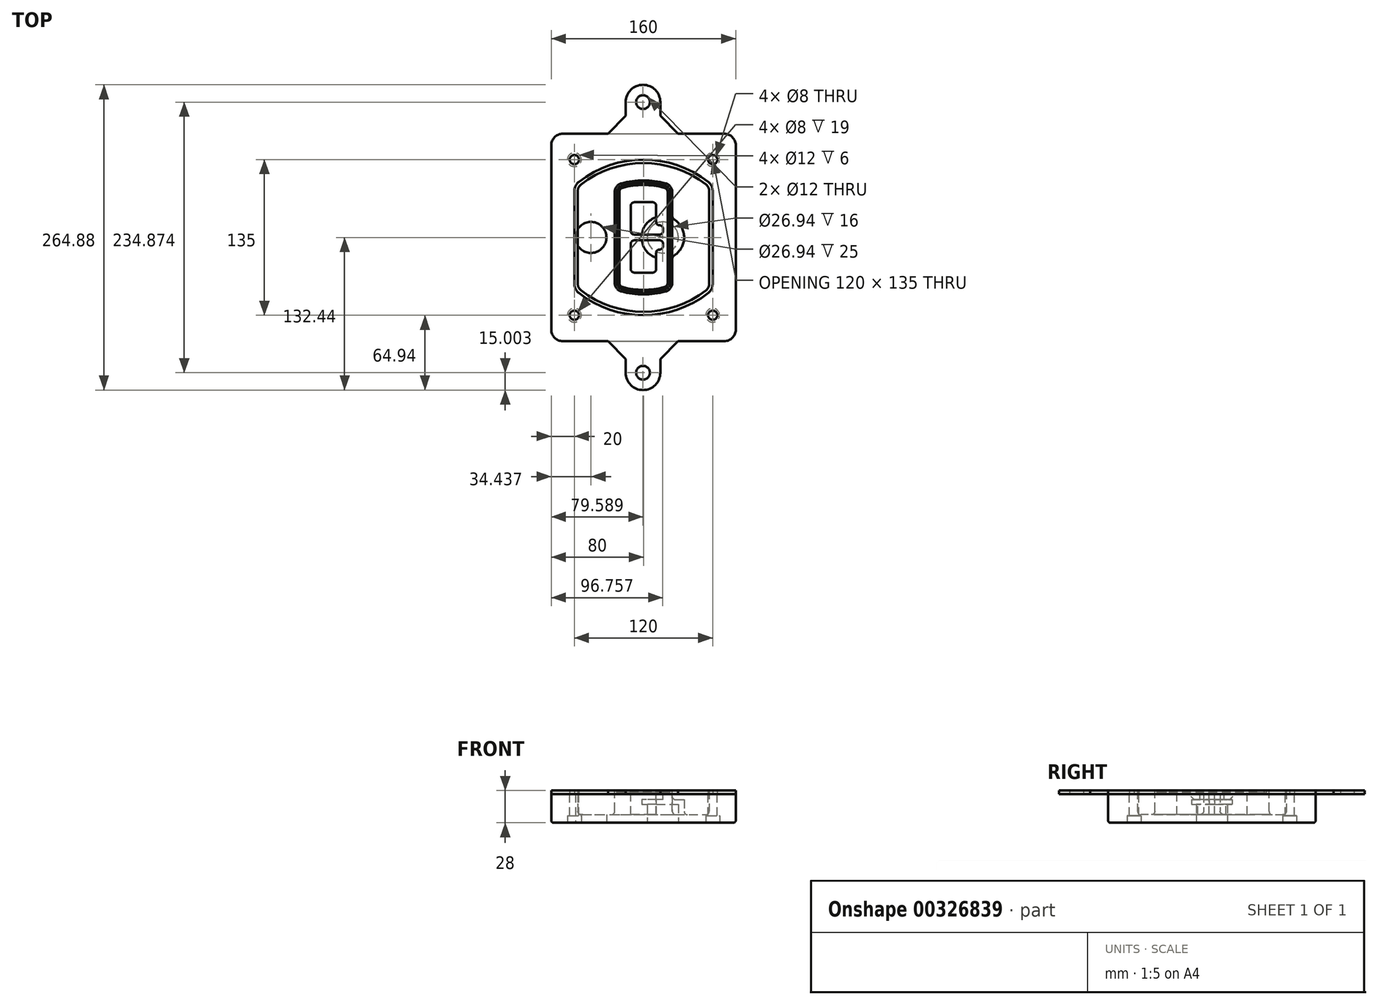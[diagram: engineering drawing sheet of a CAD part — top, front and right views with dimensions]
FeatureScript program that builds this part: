
annotation { "Feature Type Name" : "Feature", "Feature Type Description" : "" }
export const myFeature = defineFeature(function(context is Context, id is Id, definition is map)
    precondition{}
    {
        {
            var Q0;
            Q0=qCreatedBy(makeId("Top.planeOp"),FACE);
            var sketch = newSketch(context, id + "F0", { "sketchPlane" : qUnion([Q0])});
            skPoint(sketch, "E0.rect.middle", {"position": v(0, 0) * mm});
            skLineSegment(sketch, "E1.bottom", {"start": v(-70, -90) * mm, "end": v(70, -90) * mm});
            skLineSegment(sketch, "E1.top", {"start": v(-70, 90) * mm, "end": v(70, 90) * mm});
            skLineSegment(sketch, "E1.left", {"start": v(-80, -80) * mm, "end": v(-80, 80) * mm});
            skLineSegment(sketch, "E1.right", {"start": v(80, -80) * mm, "end": v(80, 80) * mm});
            skLineSegment(sketch, "E2", {"start": v(-80, 90) * mm, "end": v(80, -90) * mm, "construction": true});
            skLineSegment(sketch, "E3", {"start": v(80, 90) * mm, "end": v(-80, -90) * mm, "construction": true});
            skCircle(sketch, "E4", {"center": v(-60, 67.5) * mm, "radius": 4 * mm});
            skCircle(sketch, "E5", {"center": v(60, 67.5) * mm, "radius": 4 * mm});
            skCircle(sketch, "E6", {"center": v(60, -67.5) * mm, "radius": 4 * mm});
            skCircle(sketch, "E7", {"center": v(-60, -67.5) * mm, "radius": 4 * mm});
            skLineSegment(sketch, "E8", {"start": v(-60, 67.5) * mm, "end": v(60, 67.5) * mm, "construction": true});
            skLineSegment(sketch, "E9", {"start": v(60, 67.5) * mm, "end": v(60, -67.5) * mm, "construction": true});
            skLineSegment(sketch, "E10", {"start": v(60, -67.5) * mm, "end": v(-60, -67.5) * mm, "construction": true});
            skLineSegment(sketch, "E11", {"start": v(-60, -67.5) * mm, "end": v(-60, 67.5) * mm, "construction": true});
            skLineSegment(sketch, "E12", {"start": v(-60, 40.3) * mm, "end": v(-60, -40.3) * mm});
            skLineSegment(sketch, "E13", {"start": v(60, 40.3) * mm, "end": v(60, -40.3) * mm});
            skArc(sketch, "E14", {"start": v(56.15, 48.18) * mm, "mid": v(0, 67.5) * mm, "end": v(-56.15, 48.18) * mm});
            skArc(sketch, "E15", {"start": v(-56.15, -48.18) * mm, "mid": v(0, -67.5) * mm, "end": v(56.15, -48.18) * mm});
            skLineSegment(sketch, "E16", {"start": v(-60, 0) * mm, "end": v(60, 0) * mm, "construction": true});
            skPoint(sketch, "E17.visualSharp", {"position": v(-60, -45) * mm});
            skArc(sketch, "E17.filletArc", {"start": v(-60, -40.3) * mm, "mid": v(-58.99, -44.68) * mm, "end": v(-56.15, -48.18) * mm});
            skPoint(sketch, "E18.visualSharp", {"position": v(-60, 45) * mm});
            skArc(sketch, "E18.filletArc", {"start": v(-56.15, 48.18) * mm, "mid": v(-58.99, 44.68) * mm, "end": v(-60, 40.3) * mm});
            skPoint(sketch, "E19.visualSharp", {"position": v(60, 45) * mm});
            skArc(sketch, "E19.filletArc", {"start": v(60, 40.3) * mm, "mid": v(58.99, 44.68) * mm, "end": v(56.15, 48.18) * mm});
            skPoint(sketch, "E20.visualSharp", {"position": v(60, -45) * mm});
            skArc(sketch, "E20.filletArc", {"start": v(56.15, -48.18) * mm, "mid": v(58.99, -44.68) * mm, "end": v(60, -40.3) * mm});
            skPoint(sketch, "E21.visualSharp", {"position": v(-80, 90) * mm});
            skArc(sketch, "E21.filletArc", {"start": v(-70, 90) * mm, "mid": v(-77.07, 87.07) * mm, "end": v(-80, 80) * mm});
            skPoint(sketch, "E22.visualSharp", {"position": v(80, 90) * mm});
            skArc(sketch, "E22.filletArc", {"start": v(80, 80) * mm, "mid": v(77.07, 87.07) * mm, "end": v(70, 90) * mm});
            skPoint(sketch, "E23.visualSharp", {"position": v(80, -90) * mm});
            skArc(sketch, "E23.filletArc", {"start": v(70, -90) * mm, "mid": v(77.07, -87.07) * mm, "end": v(80, -80) * mm});
            skPoint(sketch, "E24.visualSharp", {"position": v(-80, -90) * mm});
            skArc(sketch, "E24.filletArc", {"start": v(-80, -80) * mm, "mid": v(-77.07, -87.07) * mm, "end": v(-70, -90) * mm});
            skArc(sketch, "E25.0", {"start": v(57, 40.3) * mm, "mid": v(56.3, 43.36) * mm, "end": v(54.3, 45.81) * mm});
            skLineSegment(sketch, "E25.1", {"start": v(57, 40.3) * mm, "end": v(57, -40.3) * mm});
            skArc(sketch, "E25.2", {"start": v(54.3, -45.81) * mm, "mid": v(56.3, -43.36) * mm, "end": v(57, -40.3) * mm});
            skArc(sketch, "E25.3", {"start": v(-54.3, -45.81) * mm, "mid": v(0, -64.5) * mm, "end": v(54.3, -45.81) * mm});
            skArc(sketch, "E25.4", {"start": v(-57, -40.3) * mm, "mid": v(-56.3, -43.36) * mm, "end": v(-54.3, -45.81) * mm});
            skArc(sketch, "E25.5", {"start": v(54.3, 45.81) * mm, "mid": v(0, 64.5) * mm, "end": v(-54.3, 45.81) * mm});
            skLineSegment(sketch, "E25.6", {"start": v(-57, 40.3) * mm, "end": v(-57, -40.3) * mm});
            skArc(sketch, "E25.7", {"start": v(-54.3, 45.81) * mm, "mid": v(-56.3, 43.36) * mm, "end": v(-57, 40.3) * mm});
            skArc(sketch, "E26.0", {"start": v(-58.62, 51.33) * mm, "mid": v(-62.58, 46.43) * mm, "end": v(-64, 40.3) * mm});
            skArc(sketch, "E26.1", {"start": v(58.62, 51.33) * mm, "mid": v(0, 71.5) * mm, "end": v(-58.62, 51.33) * mm});
            skArc(sketch, "E26.2", {"start": v(64, 40.3) * mm, "mid": v(62.58, 46.43) * mm, "end": v(58.62, 51.33) * mm});
            skLineSegment(sketch, "E26.3", {"start": v(64, 40.3) * mm, "end": v(64, -40.3) * mm});
            skArc(sketch, "E26.4", {"start": v(58.62, -51.33) * mm, "mid": v(62.58, -46.43) * mm, "end": v(64, -40.3) * mm});
            skLineSegment(sketch, "E26.5", {"start": v(-64, 40.3) * mm, "end": v(-64, -40.3) * mm});
            skArc(sketch, "E26.6", {"start": v(-58.62, -51.33) * mm, "mid": v(0, -71.5) * mm, "end": v(58.62, -51.33) * mm});
            skArc(sketch, "E26.7", {"start": v(-64, -40.3) * mm, "mid": v(-62.58, -46.43) * mm, "end": v(-58.62, -51.33) * mm});
            skSolve(sketch);
        }
        {
            var Q0;
            Q0=makeQuery(id+"F0.imprint","IMPRINT",FACE,{"disambiguationData":[TD([[makeQuery(id+"F0.imprint","IMPRINT",EDGE,{"derivedFrom":sQuery(id+"F0.wireOp",EDGE,"E1.bottom")}),1.0]])]});
            var Q1;
            Q1=makeQuery(id+"F0.imprint","IMPRINT",FACE,{"disambiguationData":[TD([[makeQuery(id+"F0.imprint","IMPRINT",EDGE,{"derivedFrom":sQuery(id+"F0.wireOp",EDGE,"E12")}),1.0]])]});
            var Q2;
            Q2=makeQuery(id+"F0.imprint","IMPRINT",FACE,{"disambiguationData":[TD([[makeQuery(id+"F0.imprint","IMPRINT",EDGE,{"derivedFrom":sQuery(id+"F0.wireOp",EDGE,"E25.0")}),1.0]])]});
            var Q3;
            Q3=makeQuery(id+"F0.imprint","IMPRINT",FACE,{"disambiguationData":[TD([[makeQuery(id+"F0.imprint","IMPRINT",EDGE,{"derivedFrom":sQuery(id+"F0.wireOp",EDGE,"E12")}),-1.0]])]});
            extrude(context, id + "F1", {"entities" : qUnion([Q0, Q1, Q2, Q3]), "oppositeDirection" : true, "depth" : 25 * mm});
        }
        {
            var Q0;
            Q0=makeQuery(id+"F0.imprint","IMPRINT",FACE,{"disambiguationData":[TD([[makeQuery(id+"F0.imprint","IMPRINT",EDGE,{"derivedFrom":sQuery(id+"F0.wireOp",EDGE,"E12")}),1.0]])]});
            extrude(context, id + "F2", {"entities" : qUnion([Q0]), "operationType" : NewBodyOperationType.ADD, "depth" : 3 * mm});
        }
        {
            var Q0;
            Q0=makeQuery(id+"F0.imprint","IMPRINT",FACE,{"disambiguationData":[TD([[makeQuery(id+"F0.imprint","IMPRINT",EDGE,{"derivedFrom":sQuery(id+"F0.wireOp",EDGE,"E25.0")}),1.0]])]});
            extrude(context, id + "F3", {"entities" : qUnion([Q0]), "operationType" : NewBodyOperationType.REMOVE, "oppositeDirection" : true, "depth" : 18 * mm});
        }
        {
            var Q0;
            Q0=makeQuery(id+"F2.opExtrude","CAP_FACE",FACE,{"disambiguationData":[OSD([sQuery(id+"F0.wireOp",EDGE,"E12"),sQuery(id+"F0.wireOp",EDGE,"E13"),sQuery(id+"F0.wireOp",EDGE,"E14"),sQuery(id+"F0.wireOp",EDGE,"E15"),sQuery(id+"F0.wireOp",EDGE,"E17.filletArc"),sQuery(id+"F0.wireOp",EDGE,"E18.filletArc"),sQuery(id+"F0.wireOp",EDGE,"E19.filletArc"),sQuery(id+"F0.wireOp",EDGE,"E20.filletArc"),sQuery(id+"F0.wireOp",EDGE,"E25.0"),sQuery(id+"F0.wireOp",EDGE,"E25.1"),sQuery(id+"F0.wireOp",EDGE,"E25.2"),sQuery(id+"F0.wireOp",EDGE,"E25.3"),sQuery(id+"F0.wireOp",EDGE,"E25.4"),sQuery(id+"F0.wireOp",EDGE,"E25.5"),sQuery(id+"F0.wireOp",EDGE,"E25.6"),sQuery(id+"F0.wireOp",EDGE,"E25.7")])],"isStart":false});
            var sketch = newSketch(context, id + "F4", { "sketchPlane" : qUnion([Q0])});
            skArc(sketch, "E27.0", {"start": v(-19.08, -46.97) * mm, "mid": v(0, -49.5) * mm, "end": v(19.08, -46.97) * mm});
            skArc(sketch, "E28.0", {"start": v(19.08, 46.97) * mm, "mid": v(0, 49.5) * mm, "end": v(-19.08, 46.97) * mm});
            skLineSegment(sketch, "E29", {"start": v(-25, 39.25) * mm, "end": v(-25, -39.25) * mm});
            skLineSegment(sketch, "E30", {"start": v(25, 39.25) * mm, "end": v(25, -39.25) * mm});
            skLineSegment(sketch, "E31", {"start": v(-25, 45.1) * mm, "end": v(25, 45.1) * mm, "construction": true});
            skLineSegment(sketch, "E32", {"start": v(-25, -45.1) * mm, "end": v(25, -45.1) * mm, "construction": true});
            skPoint(sketch, "E33.visualSharp", {"position": v(-25, 45.1) * mm});
            skArc(sketch, "E33.filletArc", {"start": v(-19.08, 46.97) * mm, "mid": v(-23.35, 44.11) * mm, "end": v(-25, 39.25) * mm});
            skPoint(sketch, "E34.visualSharp", {"position": v(25, 45.1) * mm});
            skArc(sketch, "E34.filletArc", {"start": v(25, 39.25) * mm, "mid": v(23.35, 44.11) * mm, "end": v(19.08, 46.97) * mm});
            skPoint(sketch, "E35.visualSharp", {"position": v(25, -45.1) * mm});
            skArc(sketch, "E35.filletArc", {"start": v(19.08, -46.97) * mm, "mid": v(23.35, -44.11) * mm, "end": v(25, -39.25) * mm});
            skPoint(sketch, "E36.visualSharp", {"position": v(-25, -45.1) * mm});
            skArc(sketch, "E36.filletArc", {"start": v(-25, -39.25) * mm, "mid": v(-23.35, -44.11) * mm, "end": v(-19.08, -46.97) * mm});
            skArc(sketch, "E37.0", {"start": v(54.3, 45.81) * mm, "mid": v(0, 64.5) * mm, "end": v(-54.3, 45.81) * mm});
            skArc(sketch, "E37.1", {"start": v(-54.3, 45.81) * mm, "mid": v(-56.3, 43.36) * mm, "end": v(-57, 40.3) * mm});
            skLineSegment(sketch, "E37.2", {"start": v(-57, 40.3) * mm, "end": v(-57, -40.3) * mm});
            skArc(sketch, "E37.3", {"start": v(-57, -40.3) * mm, "mid": v(-56.3, -43.36) * mm, "end": v(-54.3, -45.81) * mm});
            skArc(sketch, "E37.4", {"start": v(-54.3, -45.81) * mm, "mid": v(0, -64.5) * mm, "end": v(54.3, -45.81) * mm});
            skArc(sketch, "E37.5", {"start": v(54.3, -45.81) * mm, "mid": v(56.3, -43.36) * mm, "end": v(57, -40.3) * mm});
            skLineSegment(sketch, "E37.6", {"start": v(57, 40.3) * mm, "end": v(57, -40.3) * mm});
            skArc(sketch, "E37.7", {"start": v(57, 40.3) * mm, "mid": v(56.3, 43.36) * mm, "end": v(54.3, 45.81) * mm});
            skLineSegment(sketch, "E38.0", {"start": v(23, 39.25) * mm, "end": v(23, -39.25) * mm});
            skArc(sketch, "E38.1", {"start": v(18.56, -45.04) * mm, "mid": v(21.76, -42.9) * mm, "end": v(23, -39.25) * mm});
            skArc(sketch, "E38.2", {"start": v(-18.56, -45.04) * mm, "mid": v(0, -47.5) * mm, "end": v(18.56, -45.04) * mm});
            skArc(sketch, "E38.3", {"start": v(-23, -39.25) * mm, "mid": v(-21.76, -42.9) * mm, "end": v(-18.56, -45.04) * mm});
            skLineSegment(sketch, "E38.4", {"start": v(-23, 39.25) * mm, "end": v(-23, -39.25) * mm});
            skArc(sketch, "E38.5", {"start": v(23, 39.25) * mm, "mid": v(21.76, 42.9) * mm, "end": v(18.56, 45.04) * mm});
            skArc(sketch, "E38.6", {"start": v(-18.56, 45.04) * mm, "mid": v(-21.76, 42.9) * mm, "end": v(-23, 39.25) * mm});
            skArc(sketch, "E38.7", {"start": v(18.56, 45.04) * mm, "mid": v(0, 47.5) * mm, "end": v(-18.56, 45.04) * mm});
            skArc(sketch, "E39.0", {"start": v(21, 39.25) * mm, "mid": v(20.18, 41.68) * mm, "end": v(18.04, 43.1) * mm});
            skLineSegment(sketch, "E39.1", {"start": v(21, 39.25) * mm, "end": v(21, -39.25) * mm});
            skArc(sketch, "E39.2", {"start": v(18.04, -43.1) * mm, "mid": v(20.18, -41.68) * mm, "end": v(21, -39.25) * mm});
            skArc(sketch, "E39.3", {"start": v(-18.04, -43.1) * mm, "mid": v(0, -45.5) * mm, "end": v(18.04, -43.1) * mm});
            skArc(sketch, "E39.4", {"start": v(-21, -39.25) * mm, "mid": v(-20.18, -41.68) * mm, "end": v(-18.04, -43.1) * mm});
            skArc(sketch, "E39.5", {"start": v(18.04, 43.1) * mm, "mid": v(0, 45.5) * mm, "end": v(-18.04, 43.1) * mm});
            skLineSegment(sketch, "E39.6", {"start": v(-21, 39.25) * mm, "end": v(-21, -39.25) * mm});
            skArc(sketch, "E39.7", {"start": v(-18.04, 43.1) * mm, "mid": v(-20.18, 41.68) * mm, "end": v(-21, 39.25) * mm});
            skLineSegment(sketch, "E40", {"start": v(-25, 0) * mm, "end": v(25, 0) * mm, "construction": true});
            skLineSegment(sketch, "E41", {"start": v(-11, 5.5) * mm, "end": v(-11, 27.5) * mm});
            skLineSegment(sketch, "E42", {"start": v(-8, 30.5) * mm, "end": v(8, 30.5) * mm});
            skLineSegment(sketch, "E43", {"start": v(11, 27.5) * mm, "end": v(11, 13.5) * mm});
            skLineSegment(sketch, "E44", {"start": v(14, 10.5) * mm, "end": v(14, 10.5) * mm});
            skLineSegment(sketch, "E45", {"start": v(17, 7.5) * mm, "end": v(17, 5.5) * mm});
            skLineSegment(sketch, "E46", {"start": v(14, 2.5) * mm, "end": v(-8, 2.5) * mm});
            skPoint(sketch, "E47.visualSharp", {"position": v(-11, 30.5) * mm});
            skArc(sketch, "E47.filletArc", {"start": v(-8, 30.5) * mm, "mid": v(-10.12, 29.62) * mm, "end": v(-11, 27.5) * mm});
            skPoint(sketch, "E48.visualSharp", {"position": v(11, 30.5) * mm});
            skArc(sketch, "E48.filletArc", {"start": v(11, 27.5) * mm, "mid": v(10.12, 29.62) * mm, "end": v(8, 30.5) * mm});
            skPoint(sketch, "E49.visualSharp", {"position": v(11, 10.5) * mm});
            skArc(sketch, "E49.filletArc", {"start": v(11, 13.5) * mm, "mid": v(11.88, 11.38) * mm, "end": v(14, 10.5) * mm});
            skPoint(sketch, "E50.visualSharp", {"position": v(17, 10.5) * mm});
            skArc(sketch, "E50.filletArc", {"start": v(17, 7.5) * mm, "mid": v(16.12, 9.62) * mm, "end": v(14, 10.5) * mm});
            skPoint(sketch, "E51.visualSharp", {"position": v(17, 2.5) * mm});
            skArc(sketch, "E51.filletArc", {"start": v(14, 2.5) * mm, "mid": v(16.12, 3.38) * mm, "end": v(17, 5.5) * mm});
            skPoint(sketch, "E52.visualSharp", {"position": v(-11, 2.5) * mm});
            skArc(sketch, "E52.filletArc", {"start": v(-11, 5.5) * mm, "mid": v(-10.12, 3.38) * mm, "end": v(-8, 2.5) * mm});
            skLineSegment(sketch, "E53.0.MirrorCS", {"start": v(14, -2.5) * mm, "end": v(-8, -2.5) * mm});
            skArc(sketch, "E54.0.MirrorCS", {"start": v(-11, -5.5) * mm, "mid": v(-10.12, -3.38) * mm, "end": v(-8, -2.5) * mm});
            skLineSegment(sketch, "E55.0.MirrorCS", {"start": v(-11, -5.5) * mm, "end": v(-11, -27.5) * mm});
            skArc(sketch, "E56.0.MirrorCS", {"start": v(-8, -30.5) * mm, "mid": v(-10.12, -29.62) * mm, "end": v(-11, -27.5) * mm});
            skLineSegment(sketch, "E57.0.MirrorCS", {"start": v(-8, -30.5) * mm, "end": v(8, -30.5) * mm});
            skArc(sketch, "E58.0.MirrorCS", {"start": v(11, -27.5) * mm, "mid": v(10.12, -29.62) * mm, "end": v(8, -30.5) * mm});
            skLineSegment(sketch, "E59.0.MirrorCS", {"start": v(11, -27.5) * mm, "end": v(11, -13.5) * mm});
            skArc(sketch, "E60.0.MirrorCS", {"start": v(11, -13.5) * mm, "mid": v(11.88, -11.38) * mm, "end": v(14, -10.5) * mm});
            skArc(sketch, "E61.0.MirrorCS", {"start": v(17, -7.5) * mm, "mid": v(16.12, -9.62) * mm, "end": v(14, -10.5) * mm});
            skLineSegment(sketch, "E62.0.MirrorCS", {"start": v(17, -7.5) * mm, "end": v(17, -5.5) * mm});
            skArc(sketch, "E63.0.MirrorCS", {"start": v(14, -2.5) * mm, "mid": v(16.12, -3.38) * mm, "end": v(17, -5.5) * mm});
            skSolve(sketch);
        }
        {
            var Q0;
            Q0=makeQuery(id+"F4.imprint","IMPRINT",FACE,{"disambiguationData":[TD([[makeQuery(id+"F4.imprint","IMPRINT",EDGE,{"derivedFrom":sQuery(id+"F4.wireOp",EDGE,"E27.0")}),1.0]])]});
            var Q1;
            Q1=makeQuery(id+"F4.imprint","IMPRINT",FACE,{"disambiguationData":[TD([[makeQuery(id+"F4.imprint","IMPRINT",EDGE,{"derivedFrom":sQuery(id+"F4.wireOp",EDGE,"E38.0")}),-1.0]])]});
            var Q2;
            Q2=makeQuery(id+"F4.imprint","IMPRINT",FACE,{"disambiguationData":[TD([[makeQuery(id+"F4.imprint","IMPRINT",EDGE,{"derivedFrom":sQuery(id+"F4.wireOp",EDGE,"E39.0")}),1.0]])]});
            extrude(context, id + "F5", {"entities" : qUnion([Q0, Q1, Q2]), "operationType" : NewBodyOperationType.ADD, "endBound" : BoundingType.UP_TO_NEXT, "oppositeDirection" : true, "depth" : 25 * mm});
        }
        {
            var Q0;
            Q0=makeQuery(id+"F4.imprint","IMPRINT",FACE,{"disambiguationData":[TD([[makeQuery(id+"F4.imprint","IMPRINT",EDGE,{"derivedFrom":sQuery(id+"F4.wireOp",EDGE,"E38.0")}),-1.0]])]});
            extrude(context, id + "F6", {"entities" : qUnion([Q0]), "operationType" : NewBodyOperationType.REMOVE, "oppositeDirection" : true, "depth" : 2 * mm});
        }
        {
            var Q0;
            Q0=makeQuery(id+"F1.opExtrude","CAP_FACE",FACE,{"disambiguationData":[OSD([sQuery(id+"F0.wireOp",EDGE,"E1.bottom"),sQuery(id+"F0.wireOp",EDGE,"E1.top"),sQuery(id+"F0.wireOp",EDGE,"E1.left"),sQuery(id+"F0.wireOp",EDGE,"E1.right"),sQuery(id+"F0.wireOp",EDGE,"E4"),sQuery(id+"F0.wireOp",EDGE,"E5"),sQuery(id+"F0.wireOp",EDGE,"E6"),sQuery(id+"F0.wireOp",EDGE,"E7"),sQuery(id+"F0.wireOp",EDGE,"E21.filletArc"),sQuery(id+"F0.wireOp",EDGE,"E22.filletArc"),sQuery(id+"F0.wireOp",EDGE,"E23.filletArc"),sQuery(id+"F0.wireOp",EDGE,"E24.filletArc")])],"isStart":false});
            var sketch = newSketch(context, id + "F7", { "sketchPlane" : qUnion([Q0])});
            skCircle(sketch, "E64", {"center": v(16.76, 0) * mm, "radius": 13.47 * mm});
            skCircle(sketch, "E65", {"center": v(-45.56, 0) * mm, "radius": 13.47 * mm});
            skLineSegment(sketch, "E66", {"start": v(80, 0) * mm, "end": v(-80, 0) * mm});
            skCircle(sketch, "E67", {"center": v(16.76, 0) * mm, "radius": 18.47 * mm});
            skCircle(sketch, "E68", {"center": v(60, -67.5) * mm, "radius": 6 * mm});
            skCircle(sketch, "E69", {"center": v(-60, -67.5) * mm, "radius": 6 * mm});
            skCircle(sketch, "E70", {"center": v(-60, 67.5) * mm, "radius": 6 * mm});
            skCircle(sketch, "E71", {"center": v(60, 67.5) * mm, "radius": 6 * mm});
            skSolve(sketch);
        }
        {
            var Q0;
            {var subQ1=sQuery(id+"F7.wireOp",EDGE,"E66");var subQ4=sQuery(id+"F7.wireOp",EDGE,"E64");var subQ6=makeQuery(id+"F7.imprint","INTERSECT",VERTEX,{"disambiguationData":[OD(0.0)],"derivedFrom":[subQ4,subQ1]});Q0=makeQuery(id+"F7.imprint","IMPRINT",FACE,{"disambiguationData":[TD([[makeQuery(id+"F7.imprint","IMPRINT",EDGE,{"disambiguationData":[TD([[subQ6,-1.0]])],"derivedFrom":subQ4}),-1.0]])]});}
            var Q1;
            {var subQ0=sQuery(id+"F7.wireOp",EDGE,"E66");var subQ1=sQuery(id+"F7.wireOp",EDGE,"E64");var subQ3=makeQuery(id+"F7.imprint","INTERSECT",VERTEX,{"disambiguationData":[OD(0.0)],"derivedFrom":[subQ1,subQ0]});Q1=makeQuery(id+"F7.imprint","IMPRINT",FACE,{"disambiguationData":[TD([[makeQuery(id+"F7.imprint","IMPRINT",EDGE,{"disambiguationData":[TD([[subQ3,-1.0]])],"derivedFrom":subQ1}),1.0]])]});}
            var Q2;
            {var subQ0=sQuery(id+"F7.wireOp",EDGE,"E66");var subQ1=sQuery(id+"F7.wireOp",EDGE,"E64");var subQ3=makeQuery(id+"F7.imprint","INTERSECT",VERTEX,{"disambiguationData":[OD(0.0)],"derivedFrom":[subQ1,subQ0]});Q2=makeQuery(id+"F7.imprint","IMPRINT",FACE,{"disambiguationData":[TD([[makeQuery(id+"F7.imprint","IMPRINT",EDGE,{"disambiguationData":[TD([[subQ3,1.0]])],"derivedFrom":subQ1}),1.0]])]});}
            var Q3;
            {var subQ1=sQuery(id+"F7.wireOp",EDGE,"E66");var subQ4=sQuery(id+"F7.wireOp",EDGE,"E64");var subQ6=makeQuery(id+"F7.imprint","INTERSECT",VERTEX,{"disambiguationData":[OD(0.0)],"derivedFrom":[subQ4,subQ1]});Q3=makeQuery(id+"F7.imprint","IMPRINT",FACE,{"disambiguationData":[TD([[makeQuery(id+"F7.imprint","IMPRINT",EDGE,{"disambiguationData":[TD([[subQ6,1.0]])],"derivedFrom":subQ4}),-1.0]])]});}
            extrude(context, id + "F8", {"entities" : qUnion([Q0, Q1, Q2, Q3]), "operationType" : NewBodyOperationType.ADD, "oppositeDirection" : true, "depth" : 20 * mm});
        }
        {
            var Q0;
            {var subQ0=sQuery(id+"F7.wireOp",EDGE,"E66");var subQ1=sQuery(id+"F7.wireOp",EDGE,"E64");var subQ3=makeQuery(id+"F7.imprint","INTERSECT",VERTEX,{"disambiguationData":[OD(0.0)],"derivedFrom":[subQ1,subQ0]});Q0=makeQuery(id+"F7.imprint","IMPRINT",FACE,{"disambiguationData":[TD([[makeQuery(id+"F7.imprint","IMPRINT",EDGE,{"disambiguationData":[TD([[subQ3,-1.0]])],"derivedFrom":subQ1}),1.0]])]});}
            var Q1;
            {var subQ0=sQuery(id+"F7.wireOp",EDGE,"E66");var subQ1=sQuery(id+"F7.wireOp",EDGE,"E64");var subQ3=makeQuery(id+"F7.imprint","INTERSECT",VERTEX,{"disambiguationData":[OD(0.0)],"derivedFrom":[subQ1,subQ0]});Q1=makeQuery(id+"F7.imprint","IMPRINT",FACE,{"disambiguationData":[TD([[makeQuery(id+"F7.imprint","IMPRINT",EDGE,{"disambiguationData":[TD([[subQ3,1.0]])],"derivedFrom":subQ1}),1.0]])]});}
            extrude(context, id + "F9", {"entities" : qUnion([Q0, Q1]), "operationType" : NewBodyOperationType.REMOVE, "oppositeDirection" : true, "depth" : 16 * mm});
        }
        {
            var Q0;
            {var subQ0=sQuery(id+"F7.wireOp",EDGE,"E66");var subQ1=sQuery(id+"F7.wireOp",EDGE,"E65");var subQ3=makeQuery(id+"F7.imprint","INTERSECT",VERTEX,{"disambiguationData":[OD(0.0)],"derivedFrom":[subQ1,subQ0]});Q0=makeQuery(id+"F7.imprint","IMPRINT",FACE,{"disambiguationData":[TD([[makeQuery(id+"F7.imprint","IMPRINT",EDGE,{"disambiguationData":[TD([[subQ3,-1.0]])],"derivedFrom":subQ1}),1.0]])]});}
            var Q1;
            {var subQ0=sQuery(id+"F7.wireOp",EDGE,"E66");var subQ1=sQuery(id+"F7.wireOp",EDGE,"E65");var subQ3=makeQuery(id+"F7.imprint","INTERSECT",VERTEX,{"disambiguationData":[OD(0.0)],"derivedFrom":[subQ1,subQ0]});Q1=makeQuery(id+"F7.imprint","IMPRINT",FACE,{"disambiguationData":[TD([[makeQuery(id+"F7.imprint","IMPRINT",EDGE,{"disambiguationData":[TD([[subQ3,1.0]])],"derivedFrom":subQ1}),1.0]])]});}
            extrude(context, id + "F10", {"entities" : qUnion([Q0, Q1]), "operationType" : NewBodyOperationType.REMOVE, "oppositeDirection" : true, "depth" : 25 * mm});
        }
        {
            var Q0;
            Q0=makeQuery(id+"F7.imprint","IMPRINT",FACE,{"disambiguationData":[TD([[makeQuery(id+"F7.imprint","IMPRINT",EDGE,{"derivedFrom":sQuery(id+"F7.wireOp",EDGE,"E68")}),1.0]])]});
            var Q1;
            Q1=makeQuery(id+"F7.imprint","IMPRINT",FACE,{"disambiguationData":[TD([[makeQuery(id+"F7.imprint","IMPRINT",EDGE,{"derivedFrom":makeQuery(id+"F1.opExtrude","CAP_EDGE",EDGE,{"disambiguationData":[OSD([sQuery(id+"F0.wireOp",EDGE,"E5")])],"isStart":false})}),-1.0]])]});
            var Q2;
            Q2=makeQuery(id+"F7.imprint","IMPRINT",FACE,{"disambiguationData":[TD([[makeQuery(id+"F7.imprint","IMPRINT",EDGE,{"derivedFrom":sQuery(id+"F7.wireOp",EDGE,"E69")}),1.0]])]});
            var Q3;
            Q3=makeQuery(id+"F7.imprint","IMPRINT",FACE,{"disambiguationData":[TD([[makeQuery(id+"F7.imprint","IMPRINT",EDGE,{"derivedFrom":makeQuery(id+"F1.opExtrude","CAP_EDGE",EDGE,{"disambiguationData":[OSD([sQuery(id+"F0.wireOp",EDGE,"E4")])],"isStart":false})}),-1.0]])]});
            var Q4;
            Q4=makeQuery(id+"F7.imprint","IMPRINT",FACE,{"disambiguationData":[TD([[makeQuery(id+"F7.imprint","IMPRINT",EDGE,{"derivedFrom":sQuery(id+"F7.wireOp",EDGE,"E70")}),1.0]])]});
            var Q5;
            Q5=makeQuery(id+"F7.imprint","IMPRINT",FACE,{"disambiguationData":[TD([[makeQuery(id+"F7.imprint","IMPRINT",EDGE,{"derivedFrom":makeQuery(id+"F1.opExtrude","CAP_EDGE",EDGE,{"disambiguationData":[OSD([sQuery(id+"F0.wireOp",EDGE,"E7")])],"isStart":false})}),-1.0]])]});
            var Q6;
            Q6=makeQuery(id+"F7.imprint","IMPRINT",FACE,{"disambiguationData":[TD([[makeQuery(id+"F7.imprint","IMPRINT",EDGE,{"derivedFrom":sQuery(id+"F7.wireOp",EDGE,"E71")}),1.0]])]});
            var Q7;
            Q7=makeQuery(id+"F7.imprint","IMPRINT",FACE,{"disambiguationData":[TD([[makeQuery(id+"F7.imprint","IMPRINT",EDGE,{"derivedFrom":makeQuery(id+"F1.opExtrude","CAP_EDGE",EDGE,{"disambiguationData":[OSD([sQuery(id+"F0.wireOp",EDGE,"E6")])],"isStart":false})}),-1.0]])]});
            extrude(context, id + "F11", {"entities" : qUnion([Q0, Q1, Q2, Q3, Q4, Q5, Q6, Q7]), "operationType" : NewBodyOperationType.REMOVE, "oppositeDirection" : true, "depth" : 6 * mm});
        }
        {
            var Q0;
            Q0=makeQuery(id+"F9.boolean.opBoolean","COPY",FACE,{"derivedFrom":makeQuery(id+"F9.opExtrude","CAP_FACE",FACE,{"disambiguationData":[OSD([sQuery(id+"F7.wireOp",EDGE,"E64")])],"isStart":false})});
            var sketch = newSketch(context, id + "F12", { "sketchPlane" : qUnion([Q0])});
            skArc(sketch, "E72.0", {"start": v(11, 17.55) * mm, "mid": v(2.57, 11.82) * mm, "end": v(-1.54, 2.5) * mm});
            skArc(sketch, "E72.1", {"start": v(-1.54, -2.5) * mm, "mid": v(2.57, -11.82) * mm, "end": v(11, -17.55) * mm});
            skLineSegment(sketch, "E73", {"start": v(-1.54, -2.5) * mm, "end": v(14, -2.5) * mm});
            skLineSegment(sketch, "E74.0", {"start": v(14, 2.5) * mm, "end": v(-1.54, 2.5) * mm});
            skArc(sketch, "E74.1", {"start": v(14, 2.5) * mm, "mid": v(16.12, 3.38) * mm, "end": v(17, 5.5) * mm});
            skLineSegment(sketch, "E74.2", {"start": v(17, 7.5) * mm, "end": v(17, 5.5) * mm});
            skArc(sketch, "E74.3", {"start": v(17, 7.5) * mm, "mid": v(16.12, 9.62) * mm, "end": v(14, 10.5) * mm});
            skArc(sketch, "E74.4", {"start": v(11, 13.5) * mm, "mid": v(11.88, 11.38) * mm, "end": v(14, 10.5) * mm});
            skLineSegment(sketch, "E74.5", {"start": v(11, 17.55) * mm, "end": v(11, 13.5) * mm});
            skLineSegment(sketch, "E74.7", {"start": v(14, -2.5) * mm, "end": v(-1.54, -2.5) * mm});
            skArc(sketch, "E74.8", {"start": v(14, -2.5) * mm, "mid": v(16.12, -3.38) * mm, "end": v(17, -5.5) * mm});
            skLineSegment(sketch, "E74.9", {"start": v(17, -7.5) * mm, "end": v(17, -5.5) * mm});
            skArc(sketch, "E74.10", {"start": v(17, -7.5) * mm, "mid": v(16.12, -9.62) * mm, "end": v(14, -10.5) * mm});
            skArc(sketch, "E74.11", {"start": v(11, -13.5) * mm, "mid": v(11.88, -11.38) * mm, "end": v(14, -10.5) * mm});
            skLineSegment(sketch, "E74.12", {"start": v(11, -17.55) * mm, "end": v(11, -13.5) * mm});
            skPoint(sketch, "E75.orphan", {"position": v(11, -27.5) * mm});
            skPoint(sketch, "E76.orphan", {"position": v(-8, -2.5) * mm});
            skPoint(sketch, "E77.orphan", {"position": v(-8, 2.5) * mm});
            skPoint(sketch, "E78.orphan", {"position": v(11, 27.5) * mm});
            skSolve(sketch);
        }
        {
            var Q0;
            {var subQ7=sQuery(id+"F12.wireOp",EDGE,"E72.0");var subQ14=sQuery(id+"F12.wireOp",EDGE,"E72.1");var subQ16=sQuery(id+"F12.wireOp",EDGE,"E74.1");var subQ18=sQuery(id+"F12.wireOp",EDGE,"E74.8");Q0=qUnion([makeQuery(id+"F12.imprint","IMPRINT",FACE,{"disambiguationData":[TD([[makeQuery(id+"F12.imprint","IMPRINT",EDGE,{"derivedFrom":subQ7}),1.0]])]}),makeQuery(id+"F12.imprint","IMPRINT",FACE,{"disambiguationData":[TD([[makeQuery(id+"F12.imprint","IMPRINT",EDGE,{"derivedFrom":subQ14}),1.0]])]}),makeQuery(id+"F12.imprint","IMPRINT",FACE,{"disambiguationData":[TD([[makeQuery(id+"F12.imprint","IMPRINT",EDGE,{"derivedFrom":subQ16}),1.0]])]}),makeQuery(id+"F12.imprint","IMPRINT",FACE,{"disambiguationData":[TD([[makeQuery(id+"F12.imprint","IMPRINT",EDGE,{"derivedFrom":subQ18}),-1.0]])]})]);}
            var Q1;
            Q1=makeQuery(id+"F5.boolean.opBoolean","SPLIT",FACE,{"disambiguationData":[TD([makeQuery(id+"F5.opExtrude","SWEPT_FACE",FACE,{"disambiguationData":[OSD([sQuery(id+"F4.wireOp",EDGE,"E41")])]})])],"derivedFrom":makeQuery(id+"F3.boolean.opBoolean","COPY",FACE,{"derivedFrom":makeQuery(id+"F3.opExtrude","CAP_FACE",FACE,{"disambiguationData":[OSD([sQuery(id+"F0.wireOp",EDGE,"E25.0"),sQuery(id+"F0.wireOp",EDGE,"E25.1"),sQuery(id+"F0.wireOp",EDGE,"E25.2"),sQuery(id+"F0.wireOp",EDGE,"E25.3"),sQuery(id+"F0.wireOp",EDGE,"E25.4"),sQuery(id+"F0.wireOp",EDGE,"E25.5"),sQuery(id+"F0.wireOp",EDGE,"E25.6"),sQuery(id+"F0.wireOp",EDGE,"E25.7")])],"isStart":false})})});
            extrude(context, id + "F13", {"entities" : qUnion([Q0]), "operationType" : NewBodyOperationType.REMOVE, "endBound" : BoundingType.UP_TO_SURFACE, "endBoundEntityFace" : qUnion([Q1]), "depth" : 25 * mm});
        }
        {
            var Q0;
            Q0=makeQuery(id+"F3.boolean.opBoolean","COPY",EDGE,{"derivedFrom":makeQuery(id+"F3.opExtrude","CAP_EDGE",EDGE,{"disambiguationData":[OSD([sQuery(id+"F0.wireOp",EDGE,"E25.6")])],"isStart":false})});
            var Q1;
            Q1=makeQuery(id+"F8.boolean.opBoolean","INTERSECT",EDGE,{"derivedFrom":[makeQuery(id+"F5.opExtrude","SWEPT_FACE",FACE,{"disambiguationData":[OSD([sQuery(id+"F4.wireOp",EDGE,"E30")])]}),makeQuery(id+"F8.opExtrude","CAP_FACE",FACE,{"disambiguationData":[OSD([sQuery(id+"F7.wireOp",EDGE,"E67")])],"isStart":false})]});
            var Q2;
            Q2=makeQuery(id+"F8.boolean.opBoolean","INTERSECT",EDGE,{"disambiguationData":[OD(1.0)],"derivedFrom":[makeQuery(id+"F5.opExtrude","SWEPT_FACE",FACE,{"disambiguationData":[OSD([sQuery(id+"F4.wireOp",EDGE,"E30")])]}),makeQuery(id+"F8.opExtrude","SWEPT_FACE",FACE,{"disambiguationData":[OSD([sQuery(id+"F7.wireOp",EDGE,"E67")])]})]});
            var Q3;
            {var subQ0=sQuery(id+"F4.wireOp",EDGE,"E30");Q3=makeQuery(id+"F8.boolean.opBoolean","SPLIT",EDGE,{"disambiguationData":[TD([makeQuery(id+"F5.opExtrude","SWEPT_FACE",FACE,{"disambiguationData":[OSD([sQuery(id+"F4.wireOp",EDGE,"E35.filletArc")])]})])],"derivedFrom":makeQuery(id+"F5.opExtrude","CAP_EDGE",EDGE,{"disambiguationData":[OSD([subQ0])],"isStart":false})});}
            var Q4;
            {var subQ0=sQuery(id+"F0.wireOp",EDGE,"E25.7");var subQ1=sQuery(id+"F0.wireOp",EDGE,"E25.1");var subQ2=sQuery(id+"F0.wireOp",EDGE,"E25.6");var subQ3=sQuery(id+"F0.wireOp",EDGE,"E25.5");var subQ4=sQuery(id+"F0.wireOp",EDGE,"E25.4");var subQ5=sQuery(id+"F0.wireOp",EDGE,"E25.0");var subQ6=sQuery(id+"F0.wireOp",EDGE,"E25.2");var subQ7=sQuery(id+"F0.wireOp",EDGE,"E25.3");Q4=makeQuery(id+"F8.boolean.opBoolean","INTERSECT",EDGE,{"derivedFrom":[makeQuery(id+"F5.boolean.opBoolean","SPLIT",FACE,{"disambiguationData":[TD([makeQuery(id+"F2.opExtrude","SWEPT_FACE",FACE,{"disambiguationData":[OSD([subQ5])]})])],"derivedFrom":makeQuery(id+"F3.boolean.opBoolean","COPY",FACE,{"derivedFrom":makeQuery(id+"F3.opExtrude","CAP_FACE",FACE,{"disambiguationData":[OSD([subQ5,subQ1,subQ6,subQ7,subQ4,subQ3,subQ2,subQ0])],"isStart":false})})}),makeQuery(id+"F8.opExtrude","SWEPT_FACE",FACE,{"disambiguationData":[OSD([sQuery(id+"F7.wireOp",EDGE,"E67")])]})]});}
            var Q5;
            Q5=makeQuery(id+"F8.boolean.opBoolean","INTERSECT",EDGE,{"disambiguationData":[OD(0.0)],"derivedFrom":[makeQuery(id+"F5.opExtrude","SWEPT_FACE",FACE,{"disambiguationData":[OSD([sQuery(id+"F4.wireOp",EDGE,"E30")])]}),makeQuery(id+"F8.opExtrude","SWEPT_FACE",FACE,{"disambiguationData":[OSD([sQuery(id+"F7.wireOp",EDGE,"E67")])]})]});
            fillet(context, id + "F14", {"entities" : qUnion([Q0, Q1, Q2, Q3, Q4, Q5]), "radius" : 3 * mm, "tangentPropagation" : true, "allowEdgeOverflow" : false});
        }
        {
            var Q0;
            Q0=makeQuery(id+"F1.opExtrude","CAP_EDGE",EDGE,{"disambiguationData":[OSD([sQuery(id+"F0.wireOp",EDGE,"E1.bottom")])],"isStart":false});
            fillet(context, id + "F15", {"entities" : qUnion([Q0]), "radius" : 2 * mm, "tangentPropagation" : true, "allowEdgeOverflow" : false});
        }
        {
            var Q0;
            {var subQ0=sQuery(id+"F0.wireOp",EDGE,"E21.filletArc");var subQ1=sQuery(id+"F0.wireOp",EDGE,"E7");var subQ2=sQuery(id+"F0.wireOp",EDGE,"E6");var subQ3=sQuery(id+"F0.wireOp",EDGE,"E5");var subQ4=sQuery(id+"F0.wireOp",EDGE,"E4");var subQ5=sQuery(id+"F0.wireOp",EDGE,"E22.filletArc");var subQ6=sQuery(id+"F0.wireOp",EDGE,"E1.bottom");var subQ7=sQuery(id+"F0.wireOp",EDGE,"E1.right");var subQ8=sQuery(id+"F0.wireOp",EDGE,"E1.top");var subQ9=sQuery(id+"F0.wireOp",EDGE,"E1.left");var subQ10=sQuery(id+"F0.wireOp",EDGE,"E23.filletArc");var subQ11=sQuery(id+"F0.wireOp",EDGE,"E24.filletArc");Q0=makeQuery(id+"F2.boolean.opBoolean","SPLIT",FACE,{"disambiguationData":[TD([makeQuery(id+"F1.opExtrude","SWEPT_FACE",FACE,{"disambiguationData":[OSD([subQ6])]})])],"derivedFrom":makeQuery(id+"F1.opExtrude","CAP_FACE",FACE,{"disambiguationData":[OSD([subQ6,subQ8,subQ9,subQ7,subQ4,subQ3,subQ2,subQ1,subQ0,subQ5,subQ10,subQ11])],"isStart":true})});}
            var sketch = newSketch(context, id + "F16", { "sketchPlane" : qUnion([Q0])});
            skLineSegment(sketch, "E79", {"start": v(-15.41, 105.44) * mm, "end": v(-15.41, 117.44) * mm});
            skArc(sketch, "E80", {"start": v(14.59, 117.44) * mm, "mid": v(-0.41, 132.44) * mm, "end": v(-15.41, 117.44) * mm});
            skCircle(sketch, "E81", {"center": v(-0.41, 117.44) * mm, "radius": 6 * mm});
            skLineSegment(sketch, "E82", {"start": v(118.1, 0) * mm, "end": v(-115.76, 0) * mm});
            skPoint(sketch, "E82.endSnap0", {"position": v(60, 0) * mm});
            skLineSegment(sketch, "E83", {"start": v(14.59, 117.44) * mm, "end": v(14.59, 105.44) * mm});
            skLineSegment(sketch, "E84", {"start": v(14.59, 105.44) * mm, "end": v(30.03, 90) * mm});
            skLineSegment(sketch, "E85", {"start": v(-15.41, 105.44) * mm, "end": v(-30.85, 90) * mm});
            skLineSegment(sketch, "E86.MirrorCS", {"start": v(14.59, -105.44) * mm, "end": v(30.03, -90) * mm});
            skLineSegment(sketch, "E87.MirrorCS", {"start": v(14.59, -117.44) * mm, "end": v(14.59, -105.44) * mm});
            skArc(sketch, "E88.MirrorCS", {"start": v(14.59, -117.44) * mm, "mid": v(-0.41, -132.44) * mm, "end": v(-15.41, -117.44) * mm});
            skLineSegment(sketch, "E89.MirrorCS", {"start": v(-15.41, -105.44) * mm, "end": v(-15.41, -117.44) * mm});
            skLineSegment(sketch, "E90.MirrorCS", {"start": v(-15.41, -105.44) * mm, "end": v(-30.85, -90) * mm});
            skCircle(sketch, "E91.MirrorC", {"center": v(-0.41, -117.44) * mm, "radius": 6 * mm});
            skSolve(sketch);
        }
        {
            var Q0;
            {var subQ1=sQuery(id+"F16.wireOp",EDGE,"3yVoNcxS-1F8g-ADg9-q7Y3-fsagkn9f3hTi");Q0=makeQuery(id+"F16.imprint","IMPRINT",FACE,{"disambiguationData":[TD([[makeQuery(id+"F16.imprint","IMPRINT",EDGE,{"derivedFrom":subQ1}),-1.0]])]});}
            var Q1;
            {var subQ0=sQuery(id+"F16.wireOp",EDGE,"6124975b-90e3-42c7-8484-f201a9f1b6830.MirrorCS");Q1=makeQuery(id+"F16.imprint","IMPRINT",FACE,{"disambiguationData":[TD([[makeQuery(id+"F16.imprint","IMPRINT",EDGE,{"derivedFrom":subQ0}),1.0]])]});}
            var Q2;
            Q2=makeQuery(id+"F16.imprint","IMPRINT",FACE,{"disambiguationData":[TD([[makeQuery(id+"F16.imprint","IMPRINT",EDGE,{"derivedFrom":makeQuery(id+"F1.opExtrude","CAP_EDGE",EDGE,{"disambiguationData":[OSD([sQuery(id+"F0.wireOp",EDGE,"E4")])],"isStart":true})}),-1.0]])]});
            var Q3;
            Q3=makeQuery(id+"F16.imprint","IMPRINT",FACE,{"disambiguationData":[TD([[makeQuery(id+"F16.imprint","IMPRINT",EDGE,{"derivedFrom":makeQuery(id+"F1.opExtrude","CAP_EDGE",EDGE,{"disambiguationData":[OSD([sQuery(id+"F0.wireOp",EDGE,"E6")])],"isStart":true})}),-1.0]])]});
            var Q4;
            {var subQ0=sQuery(id+"F16.wireOp",EDGE,"cc54fde0-1057-406a-b5e8-0b41f291de9c0.MirrorCS");Q4=makeQuery(id+"F16.imprint","IMPRINT",FACE,{"disambiguationData":[TD([[makeQuery(id+"F16.imprint","IMPRINT",EDGE,{"derivedFrom":subQ0}),1.0]])]});}
            var Q5;
            Q5=makeQuery(id+"F16.imprint","IMPRINT",FACE,{"disambiguationData":[TD([[makeQuery(id+"F16.imprint","IMPRINT",EDGE,{"derivedFrom":sQuery(id+"F16.wireOp",EDGE,"E79")}),-1.0]])]});
            var Q6;
            {var subQ0=sQuery(id+"F16.wireOp",EDGE,"E86.MirrorCS");Q6=makeQuery(id+"F16.imprint","IMPRINT",FACE,{"disambiguationData":[TD([[makeQuery(id+"F16.imprint","IMPRINT",EDGE,{"derivedFrom":subQ0}),1.0]])]});}
            var Q7;
            Q7=makeQuery(id+"F2.opExtrude","CAP_FACE",FACE,{"disambiguationData":[OSD([sQuery(id+"F0.wireOp",EDGE,"E12"),sQuery(id+"F0.wireOp",EDGE,"E13"),sQuery(id+"F0.wireOp",EDGE,"E14"),sQuery(id+"F0.wireOp",EDGE,"E15"),sQuery(id+"F0.wireOp",EDGE,"E17.filletArc"),sQuery(id+"F0.wireOp",EDGE,"E18.filletArc"),sQuery(id+"F0.wireOp",EDGE,"E19.filletArc"),sQuery(id+"F0.wireOp",EDGE,"E20.filletArc"),sQuery(id+"F0.wireOp",EDGE,"E25.0"),sQuery(id+"F0.wireOp",EDGE,"E25.1"),sQuery(id+"F0.wireOp",EDGE,"E25.2"),sQuery(id+"F0.wireOp",EDGE,"E25.3"),sQuery(id+"F0.wireOp",EDGE,"E25.4"),sQuery(id+"F0.wireOp",EDGE,"E25.5"),sQuery(id+"F0.wireOp",EDGE,"E25.6"),sQuery(id+"F0.wireOp",EDGE,"E25.7")])],"isStart":false});
            extrude(context, id + "F17", {"entities" : qUnion([Q0, Q1, Q2, Q3, Q4, Q5, Q6]), "endBound" : BoundingType.UP_TO_SURFACE, "endBoundEntityFace" : qUnion([Q7]), "depth" : 5 * mm});
        }
    });
